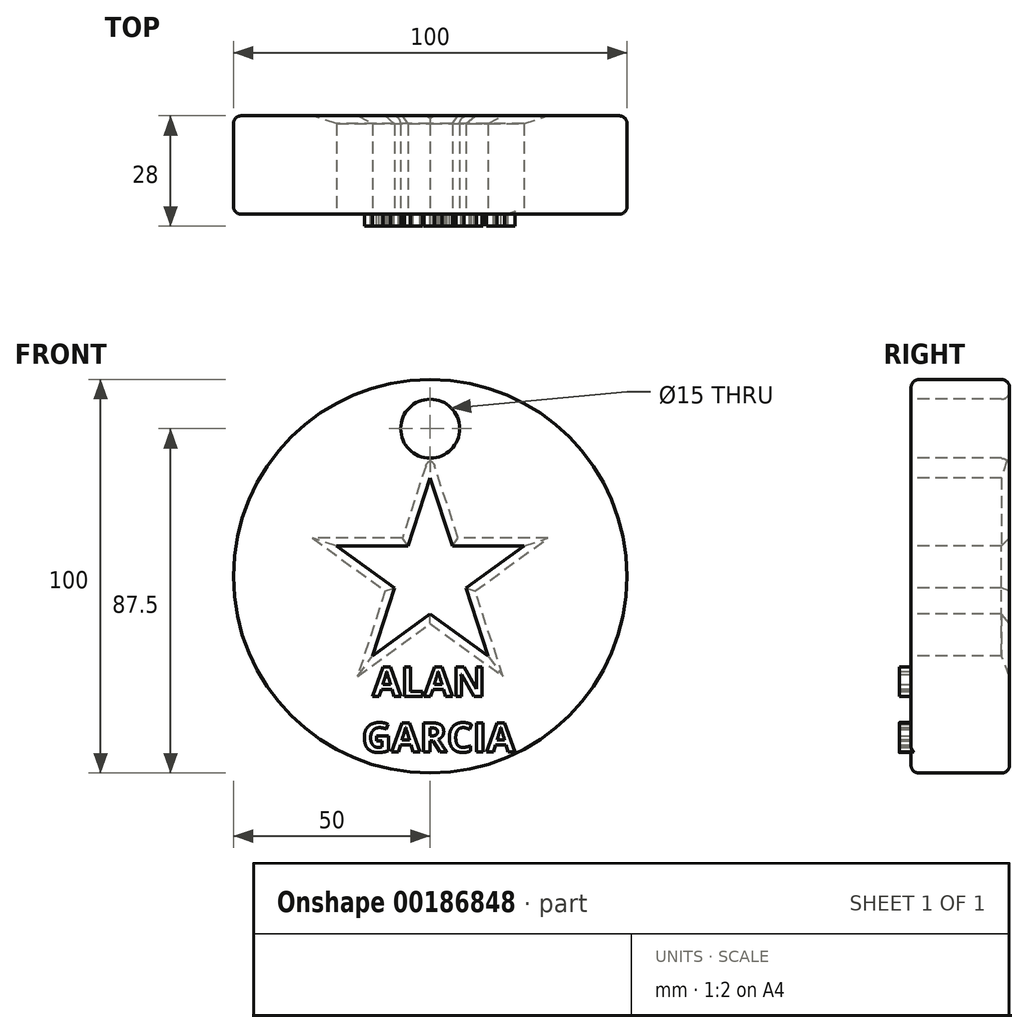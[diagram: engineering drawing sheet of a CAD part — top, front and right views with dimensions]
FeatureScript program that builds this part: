
annotation { "Feature Type Name" : "Feature", "Feature Type Description" : "" }
export const myFeature = defineFeature(function(context is Context, id is Id, definition is map)
    precondition{}
    {
        {
            var Q0;
            Q0=qCreatedBy(makeId("Front.planeOp"),FACE);
            var sketch = newSketch(context, id + "F0", { "sketchPlane" : qUnion([Q0])});
            skCircle(sketch, "E0", {"center": v(0, 0) * mm, "radius": 50 * mm});
            skSolve(sketch);
        }
        {
            var Q0;
            Q0 = qSketchRegion(id + "F0", true);
            extrude(context, id + "F1", {"entities" : qUnion([Q0]), "depth" : 12.5 * mm, "hasSecondDirection" : true, "secondDirectionOppositeDirection" : true, "secondDirectionDepth" : 12.5 * mm});
        }
        {
            var Q0;
            Q0=makeQuery(id+"F1.opExtrude","CAP_FACE",FACE,{"disambiguationData":[OSD([sQuery(id+"F0.wireOp",EDGE,"E0")])],"isStart":false});
            var sketch = newSketch(context, id + "F2", { "sketchPlane" : qUnion([Q0])});
            skCircle(sketch, "E1", {"center": v(0, 37.5) * mm, "radius": 7.5 * mm});
            skSolve(sketch);
        }
        {
            var Q0;
            Q0=makeQuery(id+"F2.imprint","IMPRINT",FACE,{"disambiguationData":[TD([[makeQuery(id+"F2.imprint","IMPRINT",EDGE,{"derivedFrom":sQuery(id+"F2.wireOp",EDGE,"E1")}),1.0]])]});
            extrude(context, id + "F3", {"entities" : qUnion([Q0]), "operationType" : NewBodyOperationType.REMOVE, "oppositeDirection" : true, "depth" : 26 * mm});
        }
        {
            var Q0;
            Q0=makeQuery(id+"F1.opExtrude","CAP_FACE",FACE,{"disambiguationData":[OSD([sQuery(id+"F0.wireOp",EDGE,"E0")])],"isStart":false});
            var sketch = newSketch(context, id + "F4", { "sketchPlane" : qUnion([Q0])});
            skArc(sketch, "E2.cCircle", {"start": v(1.57, 20.16) * mm, "mid": v(0, 20.23) * mm, "end": v(-1.57, 20.16) * mm, "construction": true});
            skLineSegment(sketch, "E2.0", {"start": v(-14.7, -20.23) * mm, "end": v(-23.78, 7.73) * mm});
            skLineSegment(sketch, "E2.1", {"start": v(-23.78, 7.73) * mm, "end": v(0, 25) * mm});
            skLineSegment(sketch, "E2.2", {"start": v(0, 25) * mm, "end": v(23.78, 7.73) * mm});
            skLineSegment(sketch, "E2.3", {"start": v(23.78, 7.73) * mm, "end": v(14.7, -20.23) * mm});
            skLineSegment(sketch, "E2.4", {"start": v(14.7, -20.23) * mm, "end": v(-14.7, -20.23) * mm});
            skPoint(sketch, "E2.0.midPoint", {"position": v(-19.24, -6.25) * mm});
            skLineSegment(sketch, "E3", {"start": v(0, 25) * mm, "end": v(-5.61, 7.73) * mm});
            skLineSegment(sketch, "E4", {"start": v(-23.78, 7.73) * mm, "end": v(-5.61, 7.73) * mm});
            skLineSegment(sketch, "E5", {"start": v(0, 25) * mm, "end": v(5.61, 7.73) * mm});
            skLineSegment(sketch, "E6", {"start": v(-14.7, -20.23) * mm, "end": v(0, -9.55) * mm});
            skLineSegment(sketch, "E7", {"start": v(-23.78, 7.73) * mm, "end": v(-9.08, -2.95) * mm});
            skLineSegment(sketch, "E8.trimOffspring", {"start": v(-9.08, -2.95) * mm, "end": v(-14.7, -20.23) * mm});
            skLineSegment(sketch, "E9.trimOffspring", {"start": v(5.61, 7.73) * mm, "end": v(23.78, 7.73) * mm});
            skLineSegment(sketch, "E10.trimOffspring", {"start": v(9.08, -2.95) * mm, "end": v(14.7, -20.23) * mm});
            skLineSegment(sketch, "E11.trimOffspring", {"start": v(9.08, -2.95) * mm, "end": v(23.78, 7.73) * mm});
            skLineSegment(sketch, "E12.trimOffspring", {"start": v(0, -9.55) * mm, "end": v(14.7, -20.23) * mm});
            skArc(sketch, "E13.trimOffspring", {"start": v(-18.7, 7.73) * mm, "mid": v(-19.24, 6.25) * mm, "end": v(-19.66, 4.74) * mm, "construction": true});
            skArc(sketch, "E14.trimOffspring", {"start": v(-13.12, -15.39) * mm, "mid": v(-11.89, -16.36) * mm, "end": v(-10.58, -17.24) * mm, "construction": true});
            skArc(sketch, "E15.trimOffspring", {"start": v(10.58, -17.24) * mm, "mid": v(11.89, -16.36) * mm, "end": v(13.12, -15.39) * mm, "construction": true});
            skArc(sketch, "E16.trimOffspring", {"start": v(19.66, 4.74) * mm, "mid": v(19.24, 6.25) * mm, "end": v(18.7, 7.73) * mm, "construction": true});
            skSolve(sketch);
        }
        {
            var Q0;
            Q0=makeQuery(id+"F4.imprint","IMPRINT",FACE,{"disambiguationData":[TD([[makeQuery(id+"F4.imprint","IMPRINT",EDGE,{"derivedFrom":sQuery(id+"F4.wireOp",EDGE,"E3")}),1.0]])]});
            extrude(context, id + "F5", {"entities" : qUnion([Q0]), "operationType" : NewBodyOperationType.REMOVE, "oppositeDirection" : true, "depth" : 26 * mm});
        }
        {
            var Q0;
            Q0=makeQuery(id+"F1.opExtrude","CAP_FACE",FACE,{"disambiguationData":[OSD([sQuery(id+"F0.wireOp",EDGE,"E0")])],"isStart":false});
            var sketch = newSketch(context, id + "F6", { "sketchPlane" : qUnion([Q0])});
            skText(sketch, "E17", { "text": " ALAN \nGARCIA", "fontName": "OpenSans-Bold.ttf"});
            const initialGuessF6  = {"E17": [-0.01736, -0.0305, 1, 0, 0.0075]};
            skSetInitialGuess(sketch, initialGuessF6);
            skSolve(sketch);
        }
        {
            var Q0;
            Q0 = qSketchRegion(id + "F6", true);
            extrude(context, id + "F7", {"entities" : qUnion([Q0]), "operationType" : NewBodyOperationType.ADD, "depth" : 3 * mm});
        }
        {
            var Q0;
            Q0=makeQuery(id+"F5.boolean.opBoolean","COPY",EDGE,{"derivedFrom":makeQuery(id+"F5.opExtrude","CAP_EDGE",EDGE,{"disambiguationData":[OSD([sQuery(id+"F4.wireOp",EDGE,"E3")])],"isStart":true})});
            var Q1;
            Q1=makeQuery(id+"F5.boolean.opBoolean","COPY",EDGE,{"derivedFrom":makeQuery(id+"F5.opExtrude","CAP_EDGE",EDGE,{"disambiguationData":[OSD([sQuery(id+"F4.wireOp",EDGE,"E5")])],"isStart":true})});
            var Q2;
            Q2=makeQuery(id+"F5.boolean.opBoolean","COPY",EDGE,{"derivedFrom":makeQuery(id+"F5.opExtrude","CAP_EDGE",EDGE,{"disambiguationData":[OSD([sQuery(id+"F4.wireOp",EDGE,"E9.trimOffspring")])],"isStart":true})});
            var Q3;
            Q3=makeQuery(id+"F5.boolean.opBoolean","COPY",EDGE,{"derivedFrom":makeQuery(id+"F5.opExtrude","CAP_EDGE",EDGE,{"disambiguationData":[OSD([sQuery(id+"F4.wireOp",EDGE,"E11.trimOffspring")])],"isStart":true})});
            var Q4;
            Q4=makeQuery(id+"F5.boolean.opBoolean","COPY",EDGE,{"derivedFrom":makeQuery(id+"F5.opExtrude","CAP_EDGE",EDGE,{"disambiguationData":[OSD([sQuery(id+"F4.wireOp",EDGE,"E10.trimOffspring")])],"isStart":true})});
            var Q5;
            Q5=makeQuery(id+"F5.boolean.opBoolean","COPY",EDGE,{"derivedFrom":makeQuery(id+"F5.opExtrude","CAP_EDGE",EDGE,{"disambiguationData":[OSD([sQuery(id+"F4.wireOp",EDGE,"E12.trimOffspring")])],"isStart":true})});
            var Q6;
            Q6=makeQuery(id+"F5.boolean.opBoolean","COPY",EDGE,{"derivedFrom":makeQuery(id+"F5.opExtrude","CAP_EDGE",EDGE,{"disambiguationData":[OSD([sQuery(id+"F4.wireOp",EDGE,"E6")])],"isStart":true})});
            var Q7;
            Q7=makeQuery(id+"F5.boolean.opBoolean","COPY",EDGE,{"derivedFrom":makeQuery(id+"F5.opExtrude","CAP_EDGE",EDGE,{"disambiguationData":[OSD([sQuery(id+"F4.wireOp",EDGE,"E8.trimOffspring")])],"isStart":true})});
            var Q8;
            Q8=makeQuery(id+"F5.boolean.opBoolean","COPY",EDGE,{"derivedFrom":makeQuery(id+"F5.opExtrude","CAP_EDGE",EDGE,{"disambiguationData":[OSD([sQuery(id+"F4.wireOp",EDGE,"E7")])],"isStart":true})});
            var Q9;
            Q9=makeQuery(id+"F5.boolean.opBoolean","COPY",EDGE,{"derivedFrom":makeQuery(id+"F5.opExtrude","CAP_EDGE",EDGE,{"disambiguationData":[OSD([sQuery(id+"F4.wireOp",EDGE,"E4")])],"isStart":true})});
            var Q10;
            Q10=makeQuery(id+"F5.boolean.opBoolean","INTERSECT",EDGE,{"derivedFrom":[makeQuery(id+"F1.opExtrude","CAP_FACE",FACE,{"disambiguationData":[OSD([sQuery(id+"F0.wireOp",EDGE,"E0")])],"isStart":true}),makeQuery(id+"F5.opExtrude","SWEPT_FACE",FACE,{"disambiguationData":[OSD([sQuery(id+"F4.wireOp",EDGE,"E5")])]})]});
            var Q11;
            Q11=makeQuery(id+"F5.boolean.opBoolean","INTERSECT",EDGE,{"derivedFrom":[makeQuery(id+"F1.opExtrude","CAP_FACE",FACE,{"disambiguationData":[OSD([sQuery(id+"F0.wireOp",EDGE,"E0")])],"isStart":true}),makeQuery(id+"F5.opExtrude","SWEPT_FACE",FACE,{"disambiguationData":[OSD([sQuery(id+"F4.wireOp",EDGE,"E3")])]})]});
            var Q12;
            Q12=makeQuery(id+"F5.boolean.opBoolean","INTERSECT",EDGE,{"derivedFrom":[makeQuery(id+"F1.opExtrude","CAP_FACE",FACE,{"disambiguationData":[OSD([sQuery(id+"F0.wireOp",EDGE,"E0")])],"isStart":true}),makeQuery(id+"F5.opExtrude","SWEPT_FACE",FACE,{"disambiguationData":[OSD([sQuery(id+"F4.wireOp",EDGE,"E4")])]})]});
            var Q13;
            Q13=makeQuery(id+"F5.boolean.opBoolean","INTERSECT",EDGE,{"derivedFrom":[makeQuery(id+"F1.opExtrude","CAP_FACE",FACE,{"disambiguationData":[OSD([sQuery(id+"F0.wireOp",EDGE,"E0")])],"isStart":true}),makeQuery(id+"F5.opExtrude","SWEPT_FACE",FACE,{"disambiguationData":[OSD([sQuery(id+"F4.wireOp",EDGE,"E7")])]})]});
            var Q14;
            Q14=makeQuery(id+"F5.boolean.opBoolean","INTERSECT",EDGE,{"derivedFrom":[makeQuery(id+"F1.opExtrude","CAP_FACE",FACE,{"disambiguationData":[OSD([sQuery(id+"F0.wireOp",EDGE,"E0")])],"isStart":true}),makeQuery(id+"F5.opExtrude","SWEPT_FACE",FACE,{"disambiguationData":[OSD([sQuery(id+"F4.wireOp",EDGE,"E8.trimOffspring")])]})]});
            var Q15;
            Q15=makeQuery(id+"F5.boolean.opBoolean","INTERSECT",EDGE,{"derivedFrom":[makeQuery(id+"F1.opExtrude","CAP_FACE",FACE,{"disambiguationData":[OSD([sQuery(id+"F0.wireOp",EDGE,"E0")])],"isStart":true}),makeQuery(id+"F5.opExtrude","SWEPT_FACE",FACE,{"disambiguationData":[OSD([sQuery(id+"F4.wireOp",EDGE,"E6")])]})]});
            var Q16;
            Q16=makeQuery(id+"F5.boolean.opBoolean","INTERSECT",EDGE,{"derivedFrom":[makeQuery(id+"F1.opExtrude","CAP_FACE",FACE,{"disambiguationData":[OSD([sQuery(id+"F0.wireOp",EDGE,"E0")])],"isStart":true}),makeQuery(id+"F5.opExtrude","SWEPT_FACE",FACE,{"disambiguationData":[OSD([sQuery(id+"F4.wireOp",EDGE,"E12.trimOffspring")])]})]});
            var Q17;
            Q17=makeQuery(id+"F5.boolean.opBoolean","INTERSECT",EDGE,{"derivedFrom":[makeQuery(id+"F1.opExtrude","CAP_FACE",FACE,{"disambiguationData":[OSD([sQuery(id+"F0.wireOp",EDGE,"E0")])],"isStart":true}),makeQuery(id+"F5.opExtrude","SWEPT_FACE",FACE,{"disambiguationData":[OSD([sQuery(id+"F4.wireOp",EDGE,"E10.trimOffspring")])]})]});
            var Q18;
            Q18=makeQuery(id+"F5.boolean.opBoolean","INTERSECT",EDGE,{"derivedFrom":[makeQuery(id+"F1.opExtrude","CAP_FACE",FACE,{"disambiguationData":[OSD([sQuery(id+"F0.wireOp",EDGE,"E0")])],"isStart":true}),makeQuery(id+"F5.opExtrude","SWEPT_FACE",FACE,{"disambiguationData":[OSD([sQuery(id+"F4.wireOp",EDGE,"E11.trimOffspring")])]})]});
            var Q19;
            Q19=makeQuery(id+"F5.boolean.opBoolean","INTERSECT",EDGE,{"derivedFrom":[makeQuery(id+"F1.opExtrude","CAP_FACE",FACE,{"disambiguationData":[OSD([sQuery(id+"F0.wireOp",EDGE,"E0")])],"isStart":true}),makeQuery(id+"F5.opExtrude","SWEPT_FACE",FACE,{"disambiguationData":[OSD([sQuery(id+"F4.wireOp",EDGE,"E9.trimOffspring")])]})]});
            chamfer(context, id + "F8", {"entities" : qUnion([Q0, Q1, Q2, Q3, Q4, Q5, Q6, Q7, Q8, Q9, Q10, Q11, Q12, Q13, Q14, Q15, Q16, Q17, Q18, Q19]), "width" : 2 * mm, "tangentPropagation" : true});
        }
        {
            var Q0;
            Q0=makeQuery(id+"F1.opExtrude","CAP_EDGE",EDGE,{"disambiguationData":[OSD([sQuery(id+"F0.wireOp",EDGE,"E0")])],"isStart":false});
            var Q1;
            Q1=makeQuery(id+"F1.opExtrude","CAP_EDGE",EDGE,{"disambiguationData":[OSD([sQuery(id+"F0.wireOp",EDGE,"E0")])],"isStart":true});
            var Q2;
            Q2=makeQuery(id+"F3.boolean.opBoolean","INTERSECT",EDGE,{"derivedFrom":[makeQuery(id+"F1.opExtrude","CAP_FACE",FACE,{"disambiguationData":[OSD([sQuery(id+"F0.wireOp",EDGE,"E0")])],"isStart":true}),makeQuery(id+"F3.opExtrude","SWEPT_FACE",FACE,{"disambiguationData":[OSD([sQuery(id+"F2.wireOp",EDGE,"E1")])]})]});
            var Q3;
            Q3=makeQuery(id+"F3.boolean.opBoolean","COPY",EDGE,{"derivedFrom":makeQuery(id+"F3.opExtrude","CAP_EDGE",EDGE,{"disambiguationData":[OSD([sQuery(id+"F2.wireOp",EDGE,"E1")])],"isStart":true})});
            fillet(context, id + "F9", {"entities" : qUnion([Q0, Q1, Q2, Q3]), "radius" : 2 * mm, "tangentPropagation" : true, "allowEdgeOverflow" : false});
        }
    });
